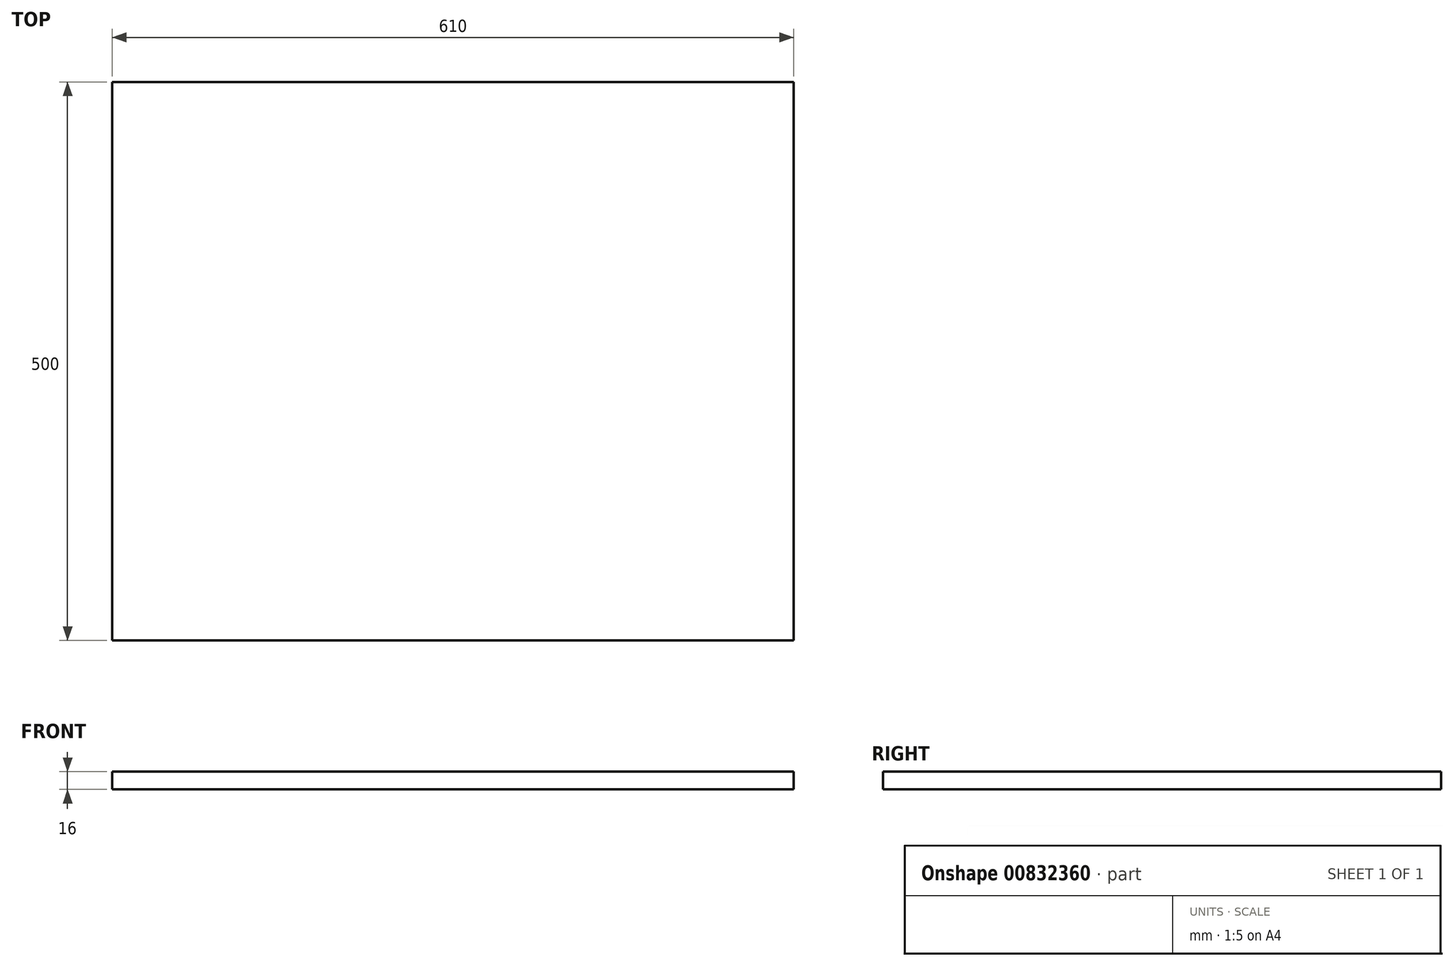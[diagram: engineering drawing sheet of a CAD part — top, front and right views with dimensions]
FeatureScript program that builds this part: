
annotation { "Feature Type Name" : "Feature", "Feature Type Description" : "" }
export const myFeature = defineFeature(function(context is Context, id is Id, definition is map)
    precondition{}
    {
        {
            var Q0;
            Q0=qCreatedBy(makeId("Top.planeOp"),FACE);
            var sketch = newSketch(context, id + "F0", { "sketchPlane" : qUnion([Q0])});
            skLineSegment(sketch, "E0.bottom", {"start": v(0, 0) * mm, "end": v(610, 0) * mm});
            skLineSegment(sketch, "E0.top", {"start": v(0, 500) * mm, "end": v(610, 500) * mm});
            skLineSegment(sketch, "E0.left", {"start": v(0, 0) * mm, "end": v(0, 500) * mm});
            skLineSegment(sketch, "E0.right", {"start": v(610, 0) * mm, "end": v(610, 500) * mm});
            skSolve(sketch);
        }
        {
            var Q0;
            Q0=makeQuery(id+"F0.imprint","IMPRINT",FACE,{"disambiguationData":[TD([[makeQuery(id+"F0.imprint","IMPRINT",EDGE,{"derivedFrom":sQuery(id+"F0.wireOp",EDGE,"E0.bottom")}),1.0]])]});
            extrude(context, id + "F1", {"entities" : qUnion([Q0]), "depth" : 16 * mm, "offsetDistance" : 25 * mm});
        }
    });
